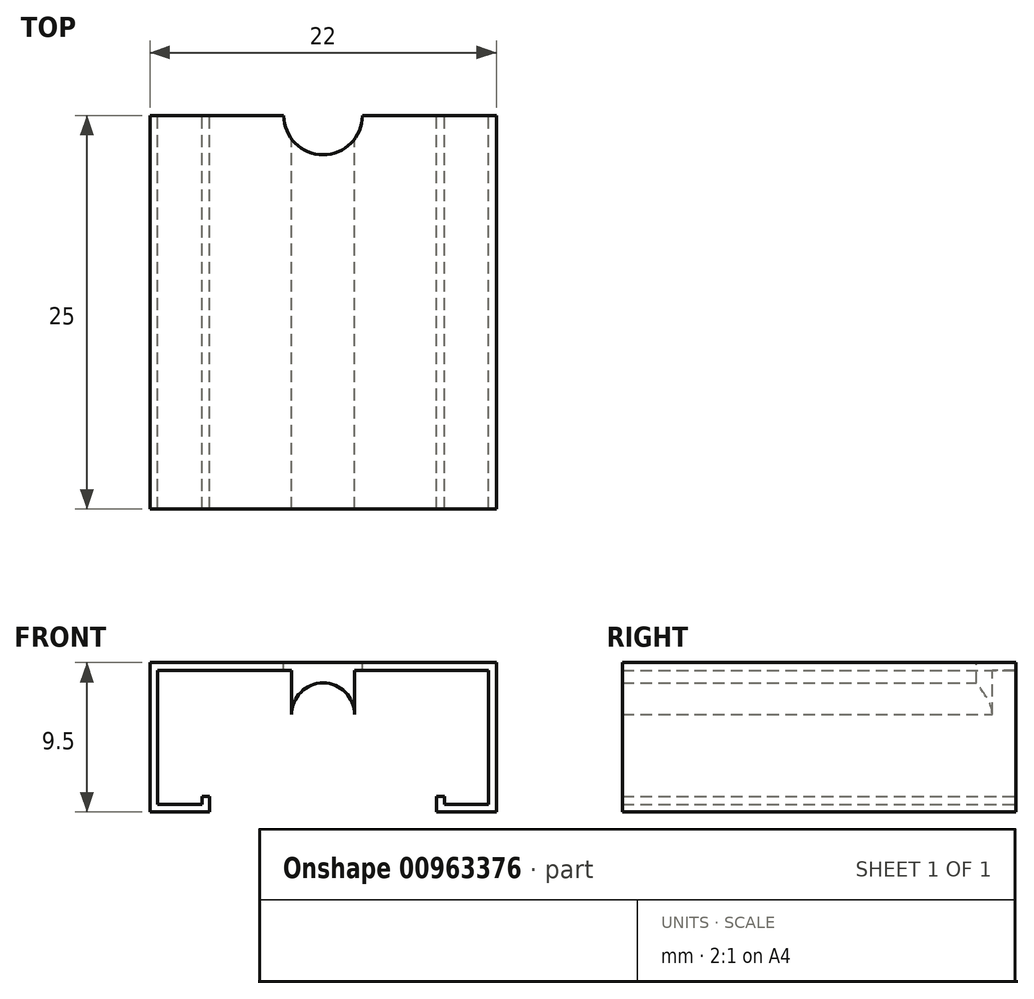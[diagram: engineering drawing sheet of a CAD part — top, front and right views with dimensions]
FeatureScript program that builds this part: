
annotation { "Feature Type Name" : "Feature", "Feature Type Description" : "" }
export const myFeature = defineFeature(function(context is Context, id is Id, definition is map)
    precondition{}
    {
        {
            var Q0;
            Q0=qCreatedBy(makeId("Front.planeOp"),FACE);
            var sketch = newSketch(context, id + "F0", { "sketchPlane" : qUnion([Q0])});
            skLineSegment(sketch, "E0", {"start": v(-10.5, 0) * mm, "end": v(-10.5, 8.5) * mm});
            skLineSegment(sketch, "E1", {"start": v(-10.5, 8.5) * mm, "end": v(0, 8.5) * mm});
            skLineSegment(sketch, "E2", {"start": v(0, 8.5) * mm, "end": v(10.5, 8.5) * mm});
            skLineSegment(sketch, "E3", {"start": v(10.5, 8.5) * mm, "end": v(10.5, 0) * mm});
            skLineSegment(sketch, "E4", {"start": v(10.5, 0) * mm, "end": v(11, 0) * mm});
            skLineSegment(sketch, "E5", {"start": v(11, 0) * mm, "end": v(11, 9) * mm});
            skLineSegment(sketch, "E6", {"start": v(11, 9) * mm, "end": v(0, 9) * mm});
            skLineSegment(sketch, "E7", {"start": v(0, 9) * mm, "end": v(-11, 9) * mm});
            skLineSegment(sketch, "E8", {"start": v(-11, 9) * mm, "end": v(-11, 0) * mm});
            skLineSegment(sketch, "E9", {"start": v(-11, 0) * mm, "end": v(-10.5, 0) * mm});
            skLineSegment(sketch, "E10", {"start": v(0, 8.5) * mm, "end": v(0, 9) * mm, "construction": true});
            skLineSegment(sketch, "E11.bottom", {"start": v(-2, 8.5) * mm, "end": v(2, 8.5) * mm});
            skLineSegment(sketch, "E11.top", {"start": v(-2, 5.7) * mm, "end": v(2, 5.7) * mm, "construction": true});
            skLineSegment(sketch, "E11.left", {"start": v(-2, 8.5) * mm, "end": v(-2, 5.7) * mm});
            skLineSegment(sketch, "E11.right", {"start": v(2, 8.5) * mm, "end": v(2, 5.7) * mm});
            skPoint(sketch, "E12", {"position": v(0, 5.7) * mm});
            skLineSegment(sketch, "E13", {"start": v(10.5, 0) * mm, "end": v(7.7, 0) * mm});
            skLineSegment(sketch, "E14", {"start": v(7.7, 0) * mm, "end": v(7.7, 0.5) * mm});
            skLineSegment(sketch, "E15", {"start": v(7.7, 0.5) * mm, "end": v(7.2, 0.5) * mm});
            skLineSegment(sketch, "E16", {"start": v(7.2, 0.5) * mm, "end": v(7.2, -0.5) * mm});
            skLineSegment(sketch, "E17", {"start": v(7.2, -0.5) * mm, "end": v(11, -0.5) * mm});
            skLineSegment(sketch, "E18", {"start": v(11, -0.5) * mm, "end": v(11, 0) * mm});
            skLineSegment(sketch, "E19", {"start": v(-10.5, 0) * mm, "end": v(-7.7, 0) * mm});
            skLineSegment(sketch, "E20", {"start": v(-7.7, 0) * mm, "end": v(-7.7, 0.5) * mm});
            skLineSegment(sketch, "E21", {"start": v(-7.7, 0.5) * mm, "end": v(-7.2, 0.5) * mm});
            skLineSegment(sketch, "E22", {"start": v(-7.2, 0.5) * mm, "end": v(-7.2, -0.5) * mm});
            skLineSegment(sketch, "E23", {"start": v(-7.2, -0.5) * mm, "end": v(-11, -0.5) * mm});
            skLineSegment(sketch, "E24", {"start": v(-11, -0.5) * mm, "end": v(-11, 0) * mm});
            skArc(sketch, "E25", {"start": v(2, 5.7) * mm, "mid": v(0, 7.7) * mm, "end": v(-2, 5.7) * mm});
            skSolve(sketch);
        }
        {
            var Q0;
            Q0 = qSketchRegion(id + "F0", true);
            extrude(context, id + "F1", {"entities" : qUnion([Q0]), "depth" : 25 * mm, "offsetDistance" : 25 * mm});
        }
        {
            var Q0;
            Q0=makeQuery(id+"F1.opExtrude","SWEPT_FACE",FACE,{"disambiguationData":[OSD([sQuery(id+"F0.wireOp",EDGE,"E6"),sQuery(id+"F0.wireOp",EDGE,"E7")])]});
            var sketch = newSketch(context, id + "F2", { "sketchPlane" : qUnion([Q0])});
            skArc(sketch, "E26", {"start": v(-2.5, 0) * mm, "mid": v(0, -2.5) * mm, "end": v(2.5, 0) * mm});
            skLineSegment(sketch, "E27", {"start": v(-2.5, 0) * mm, "end": v(0, 0) * mm});
            skLineSegment(sketch, "E28", {"start": v(0, 0) * mm, "end": v(2.5, 0) * mm});
            skLineSegment(sketch, "E29", {"start": v(0, 0) * mm, "end": v(0, -2.5) * mm, "construction": true});
            skSolve(sketch);
        }
        {
            var Q0;
            Q0 = qSketchRegion(id + "F2", true);
            extrude(context, id + "F3", {"entities" : qUnion([Q0]), "operationType" : NewBodyOperationType.REMOVE, "endBound" : BoundingType.THROUGH_ALL, "oppositeDirection" : true, "depth" : 25 * mm, "offsetDistance" : 25 * mm});
        }
    });
